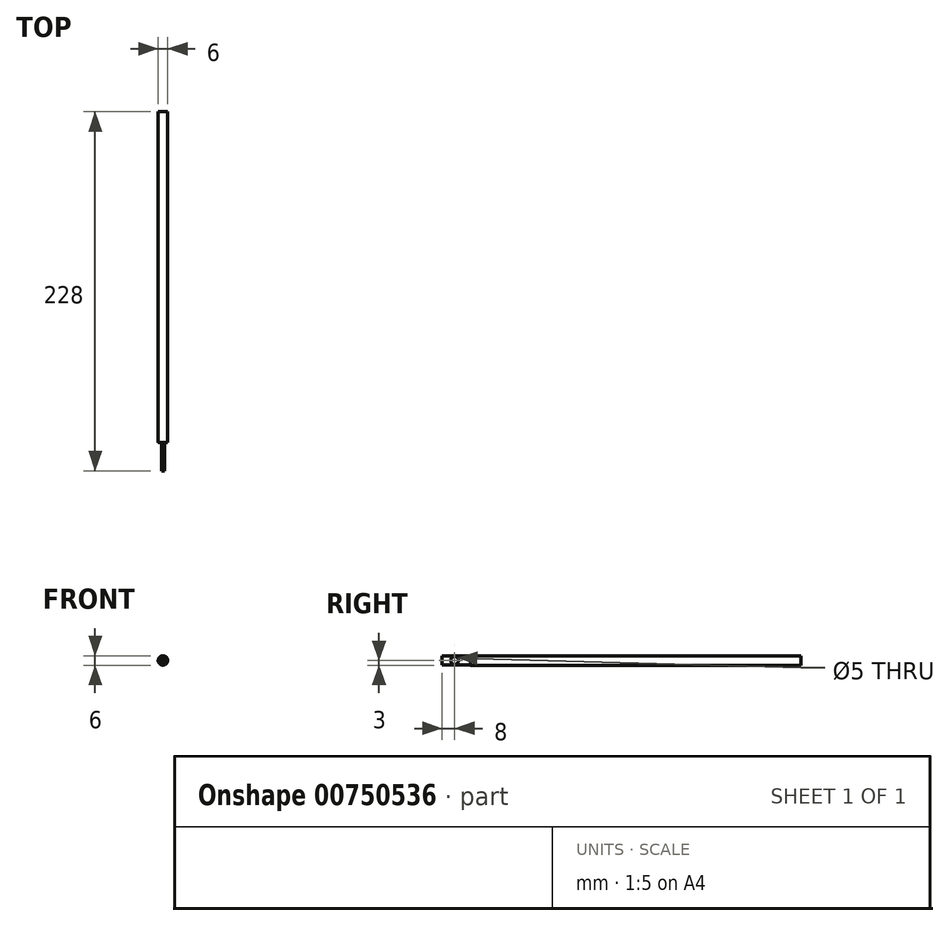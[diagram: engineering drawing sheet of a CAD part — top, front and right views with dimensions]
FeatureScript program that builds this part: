
annotation { "Feature Type Name" : "Feature", "Feature Type Description" : "" }
export const myFeature = defineFeature(function(context is Context, id is Id, definition is map)
    precondition{}
    {
        {
            var Q0;
            Q0=qCreatedBy(makeId("Front.planeOp"),FACE);
            var sketch = newSketch(context, id + "F0", { "sketchPlane" : qUnion([Q0])});
            skCircle(sketch, "E0", {"center": v(0, 0) * mm, "radius": 3 * mm});
            skSolve(sketch);
        }
        {
            var Q0;
            Q0 = qSketchRegion(id + "F0", true);
            extrude(context, id + "F1", {"entities" : qUnion([Q0]), "depth" : 210 * mm, "offsetDistance" : 25 * mm});
        }
        {
            var Q0;
            Q0=makeQuery(id+"F1.opExtrude","CAP_FACE",FACE,{"disambiguationData":[OSD([sQuery(id+"F0.wireOp",EDGE,"E0")])],"isStart":false});
            var sketch = newSketch(context, id + "F2", { "sketchPlane" : qUnion([Q0])});
            skLineSegment(sketch, "E1.bottom", {"start": v(-0.92, -2.86) * mm, "end": v(0.92, -2.86) * mm});
            skLineSegment(sketch, "E1.top", {"start": v(-0.92, 2.86) * mm, "end": v(0.92, 2.86) * mm});
            skLineSegment(sketch, "E1.left", {"start": v(-0.92, -2.86) * mm, "end": v(-0.92, 2.86) * mm});
            skLineSegment(sketch, "E1.right", {"start": v(0.92, -2.86) * mm, "end": v(0.92, 2.86) * mm});
            skPoint(sketch, "E1.middle", {"position": v(0, 0) * mm});
            skSolve(sketch);
        }
        {
            var Q0;
            Q0 = qSketchRegion(id + "F2", true);
            extrude(context, id + "F3", {"entities" : qUnion([Q0]), "operationType" : NewBodyOperationType.ADD, "depth" : 18 * mm, "offsetDistance" : 25 * mm});
        }
        {
            var Q0;
            Q0=makeQuery(id+"F3.opExtrude","SWEPT_FACE",FACE,{"disambiguationData":[OSD([sQuery(id+"F2.wireOp",EDGE,"E1.right")])]});
            var sketch = newSketch(context, id + "F4", { "sketchPlane" : qUnion([Q0])});
            skCircle(sketch, "E2", {"center": v(-220, 0) * mm, "radius": 2.5 * mm});
            skPoint(sketch, "E2.centerSnap0", {"position": v(-228, 0) * mm});
            skSolve(sketch);
        }
        {
            var Q0;
            {var subQ0=sQuery(id+"F2.wireOp",EDGE,"E1.right");Q0=makeQuery(id+"F4.imprint","IMPRINT",FACE,{"disambiguationData":[TD([[makeQuery(id+"F4.imprint","IMPRINT",EDGE,{"derivedFrom":makeQuery(id+"F3.opExtrude","CAP_EDGE",EDGE,{"disambiguationData":[OSD([subQ0])],"isStart":false})}),-1.0]])]});}
            var sketch = newSketch(context, id + "F5", { "sketchPlane" : qUnion([Q0])});
            skSolve(sketch);
        }
        {
            var Q0;
            Q0=makeQuery(id+"F5.imprint","IMPRINT",FACE,{"disambiguationData":[TD([[makeQuery(id+"F5.imprint","IMPRINT",EDGE,{"derivedFrom":makeQuery(id+"F4.imprint","IMPRINT",EDGE,{"derivedFrom":sQuery(id+"F4.wireOp",EDGE,"E2")})}),1.0]])]});
            var Q1;
            Q1=sQuery(id+"F4.wireOp",EDGE,"E2");
            extrude(context, id + "F6", {"entities" : qUnion([Q0]), "operationType" : NewBodyOperationType.REMOVE, "surfaceEntities" : qUnion([Q1]), "endBound" : BoundingType.UP_TO_NEXT, "oppositeDirection" : true, "depth" : 25 * mm, "offsetDistance" : 25 * mm});
        }
    });
